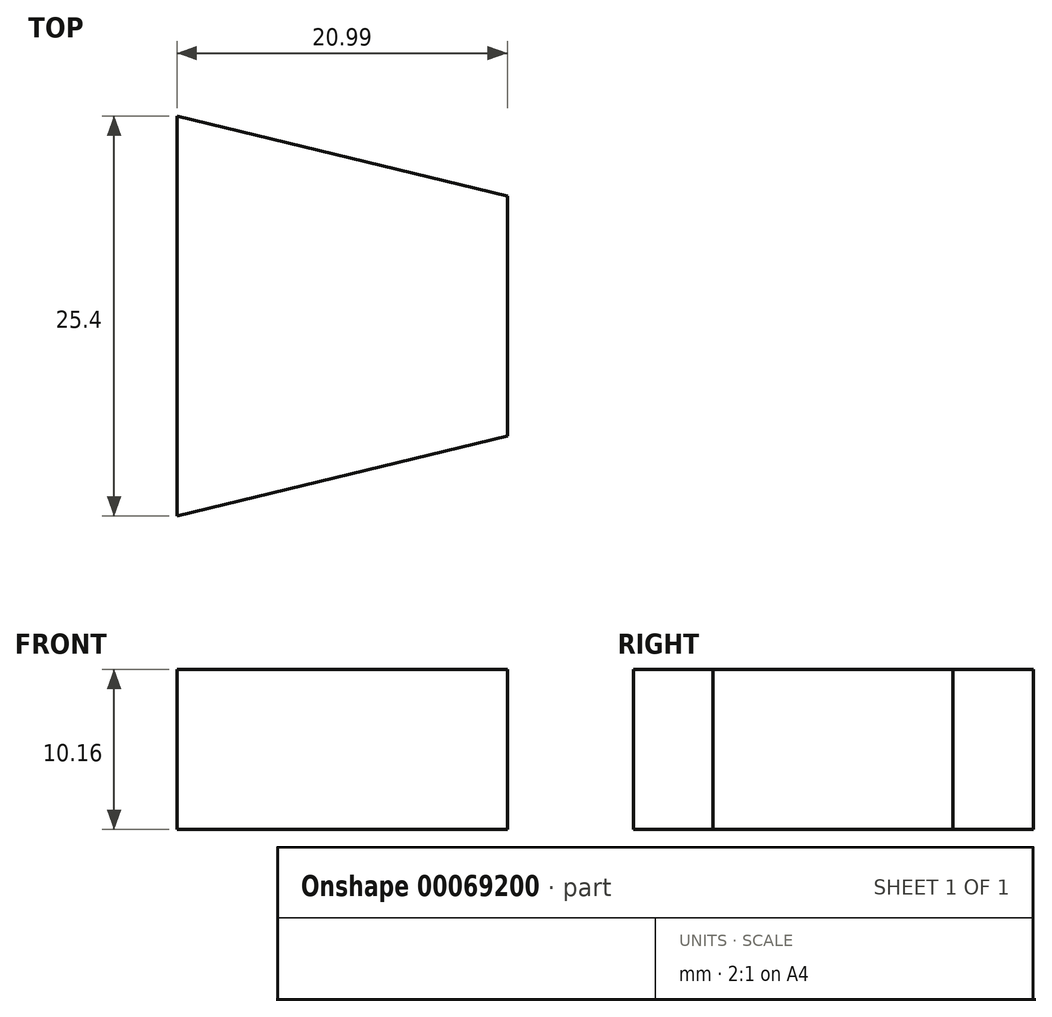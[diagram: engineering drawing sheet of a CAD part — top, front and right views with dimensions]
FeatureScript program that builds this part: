
annotation { "Feature Type Name" : "Feature", "Feature Type Description" : "" }
export const myFeature = defineFeature(function(context is Context, id is Id, definition is map)
    precondition{}
    {
        {
            var Q0;
            Q0=qCreatedBy(makeId("Top.planeOp"),FACE);
            var sketch = newSketch(context, id + "F0", { "sketchPlane" : qUnion([Q0])});
            skLineSegment(sketch, "E0", {"start": v(0, 10.15) * mm, "end": v(20.99, 5.06) * mm});
            skLineSegment(sketch, "E1", {"start": v(20.99, 5.06) * mm, "end": v(20.99, -10.18) * mm});
            skLineSegment(sketch, "E2", {"start": v(20.99, -10.18) * mm, "end": v(0, -15.25) * mm});
            skLineSegment(sketch, "E3", {"start": v(0, 10.15) * mm, "end": v(0, -15.25) * mm});
            skSolve(sketch);
        }
        {
            var Q0;
            Q0 = qSketchRegion(id + "F0", true);
            extrude(context, id + "F1", {"entities" : qUnion([Q0]), "depth" : 10.16 * mm});
        }
    });
